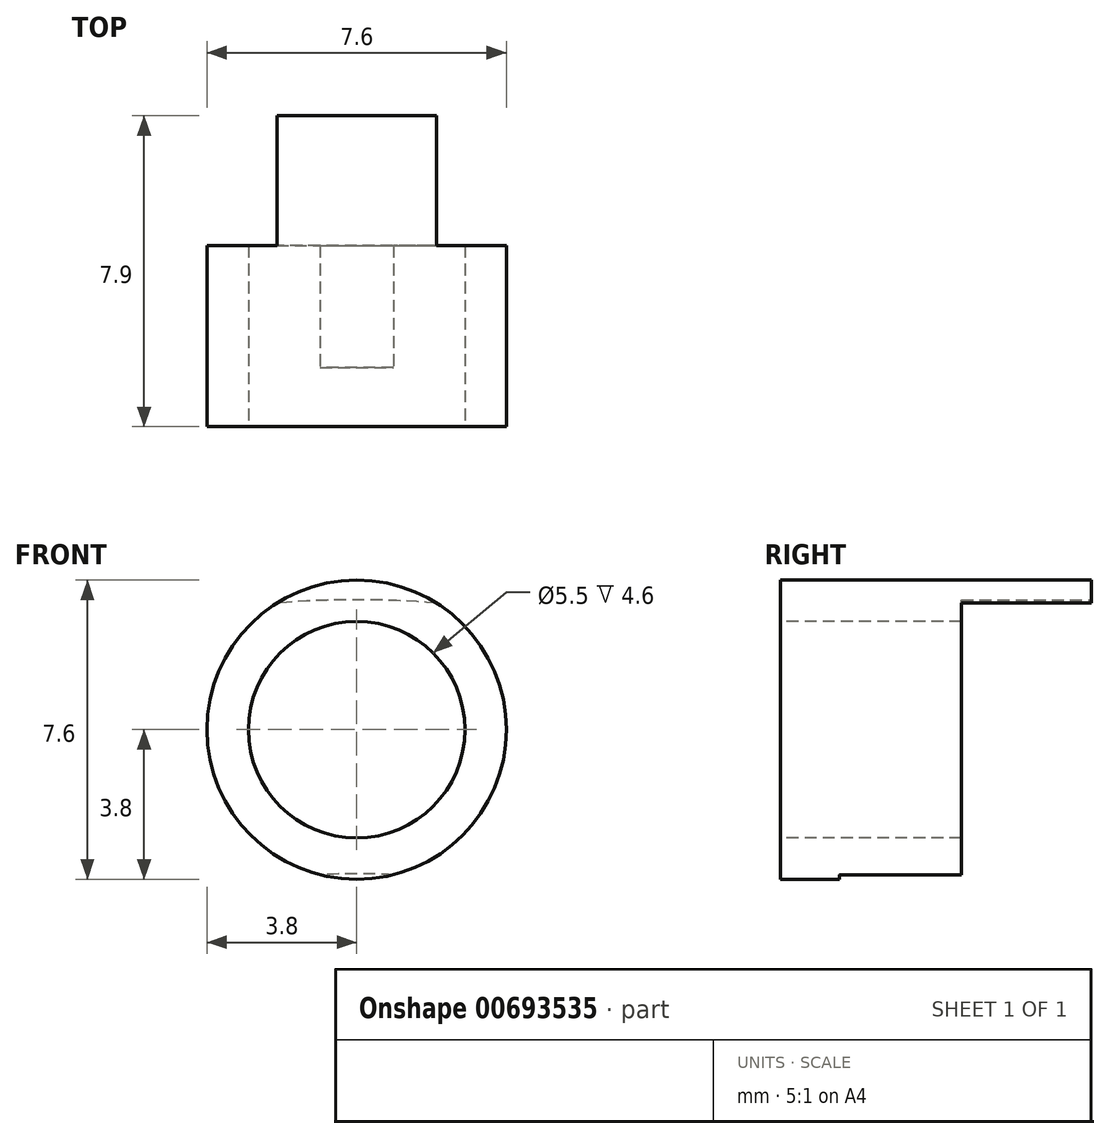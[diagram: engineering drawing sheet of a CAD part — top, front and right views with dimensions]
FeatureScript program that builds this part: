
annotation { "Feature Type Name" : "Feature", "Feature Type Description" : "" }
export const myFeature = defineFeature(function(context is Context, id is Id, definition is map)
    precondition{}
    {
        {
            var Q0;
            Q0=qCreatedBy(makeId("Front.planeOp"),FACE);
            var sketch = newSketch(context, id + "F0", { "sketchPlane" : qUnion([Q0])});
            skCircle(sketch, "E0", {"center": v(0, 0) * mm, "radius": 15.72 * mm});
            skCircle(sketch, "E1", {"center": v(0, 0) * mm, "radius": 26.35 * mm});
            skSolve(sketch);
        }
        {
            var Q0;
            Q0=makeQuery(id+"F0.imprint","IMPRINT",FACE,{"disambiguationData":[TD([[makeQuery(id+"F0.imprint","IMPRINT",EDGE,{"derivedFrom":sQuery(id+"F0.wireOp",EDGE,"E0")}),-1.0]])]});
            extrude(context, id + "F1", {"entities" : qUnion([Q0]), "depth" : 11.3 * mm, "offsetDistance" : 25 * mm});
        }
        {
            var Q0;
            Q0=makeQuery(id+"F1.opExtrude","CAP_FACE",FACE,{"disambiguationData":[OSD([sQuery(id+"F0.wireOp",EDGE,"E0"),sQuery(id+"F0.wireOp",EDGE,"E1")])],"isStart":true});
            var sketch = newSketch(context, id + "F2", { "sketchPlane" : qUnion([Q0])});
            skCircle(sketch, "E2", {"center": v(0, 0) * mm, "radius": 17.39 * mm});
            skSolve(sketch);
        }
        {
            var Q0;
            Q0=makeQuery(id+"F2.imprint","IMPRINT",FACE,{"disambiguationData":[TD([[makeQuery(id+"F2.imprint","IMPRINT",EDGE,{"derivedFrom":sQuery(id+"F2.wireOp",EDGE,"E2")}),1.0]])]});
            extrude(context, id + "F3", {"entities" : qUnion([Q0]), "operationType" : NewBodyOperationType.REMOVE, "oppositeDirection" : true, "depth" : 6.4 * mm, "offsetDistance" : 25 * mm});
        }
        {
            var Q0;
            Q0=makeQuery(id+"F1.opExtrude","CAP_FACE",FACE,{"disambiguationData":[OSD([sQuery(id+"F0.wireOp",EDGE,"E0"),sQuery(id+"F0.wireOp",EDGE,"E1")])],"isStart":true});
            var sketch = newSketch(context, id + "F4", { "sketchPlane" : qUnion([Q0])});
            skCircle(sketch, "E3", {"center": v(0, 0) * mm, "radius": 24.35 * mm});
            skSolve(sketch);
        }
        {
            var Q0;
            Q0=makeQuery(id+"F4.imprint","IMPRINT",FACE,{"disambiguationData":[TD([[makeQuery(id+"F4.imprint","IMPRINT",EDGE,{"derivedFrom":sQuery(id+"F4.wireOp",EDGE,"E3")}),1.0]])]});
            extrude(context, id + "F5", {"entities" : qUnion([Q0]), "operationType" : NewBodyOperationType.REMOVE, "oppositeDirection" : true, "depth" : 3.3 * mm, "offsetDistance" : 25 * mm});
        }
        {
            var Q0;
            Q0=makeQuery(id+"F1.opExtrude","CAP_FACE",FACE,{"disambiguationData":[OSD([sQuery(id+"F0.wireOp",EDGE,"E0"),sQuery(id+"F0.wireOp",EDGE,"E1")])],"isStart":false});
            var sketch = newSketch(context, id + "F6", { "sketchPlane" : qUnion([Q0])});
            skCircle(sketch, "E4", {"center": v(0, 21.05) * mm, "radius": 2.75 * mm});
            skCircle(sketch, "E5", {"center": v(0, 21.05) * mm, "radius": 3.8 * mm});
            skSolve(sketch);
        }
        {
            var Q0;
            Q0=makeQuery(id+"F6.imprint","IMPRINT",FACE,{"disambiguationData":[TD([[makeQuery(id+"F6.imprint","IMPRINT",EDGE,{"derivedFrom":sQuery(id+"F6.wireOp",EDGE,"E4")}),-1.0]])]});
            extrude(context, id + "F7", {"entities" : qUnion([Q0]), "operationType" : NewBodyOperationType.REMOVE, "oppositeDirection" : true, "depth" : 3.4 * mm, "offsetDistance" : 25 * mm});
        }
        {
            var Q0;
            Q0=makeQuery(id+"F7.boolean.opBoolean","SPLIT",FACE,{"disambiguationData":[TD([makeQuery(id+"F7.opExtrude","SWEPT_FACE",FACE,{"disambiguationData":[OSD([sQuery(id+"F6.wireOp",EDGE,"E4")])]})])],"derivedFrom":makeQuery(id+"F1.opExtrude","CAP_FACE",FACE,{"disambiguationData":[OSD([sQuery(id+"F0.wireOp",EDGE,"E0"),sQuery(id+"F0.wireOp",EDGE,"E1")])],"isStart":false})});
            extrude(context, id + "F8", {"entities" : qUnion([Q0]), "operationType" : NewBodyOperationType.REMOVE, "oppositeDirection" : true, "depth" : 10 * mm, "offsetDistance" : 25 * mm});
        }
        {
            var Q0;
            Q0=qCreatedBy(makeId("Right.planeOp"),FACE);
            var sketch = newSketch(context, id + "F9", { "sketchPlane" : qUnion([Q0])});
            skLineSegment(sketch, "E6", {"start": v(37.37, 0) * mm, "end": v(-51.59, 0) * mm});
            skSolve(sketch);
        }
        {
            var Q0;
            {var subQ0=sQuery(id+"F0.wireOp",EDGE,"E0");var subQ1=sQuery(id+"F0.wireOp",EDGE,"E1");Q0=makeQuery(id+"FGy4sFd92jukGps_1.1.F7.boolean.opBoolean","SPLIT",FACE,{"disambiguationData":[TD([makeQuery(id+"FGy4sFd92jukGps_1.1.F7.opExtrude","SWEPT_FACE",FACE,{"disambiguationData":[OSD([sQuery(id+"F6.wireOp",EDGE,"E4")])]})])],"derivedFrom":makeQuery(id+"F7.boolean.opBoolean","SPLIT",FACE,{"disambiguationData":[TD([makeQuery(id+"F1.opExtrude","SWEPT_FACE",FACE,{"disambiguationData":[OSD([subQ0])]})])],"derivedFrom":makeQuery(id+"F1.opExtrude","CAP_FACE",FACE,{"disambiguationData":[OSD([subQ0,subQ1])],"isStart":false})})});}
            var Q1;
            {var subQ0=sQuery(id+"F0.wireOp",EDGE,"E0");var subQ1=makeQuery(id+"F1.opExtrude","SWEPT_FACE",FACE,{"disambiguationData":[OSD([subQ0])]});var subQ2=sQuery(id+"F0.wireOp",EDGE,"E1");Q1=makeQuery(id+"FGy4sFd92jukGps_1.2.F7.boolean.opBoolean","SPLIT",FACE,{"disambiguationData":[TD([makeQuery(id+"FGy4sFd92jukGps_1.2.F7.opExtrude","SWEPT_FACE",FACE,{"disambiguationData":[OSD([sQuery(id+"F6.wireOp",EDGE,"E4")])]})])],"derivedFrom":makeQuery(id+"FGy4sFd92jukGps_1.1.F7.boolean.opBoolean","SPLIT",FACE,{"disambiguationData":[TD([subQ1])],"derivedFrom":makeQuery(id+"F7.boolean.opBoolean","SPLIT",FACE,{"disambiguationData":[TD([subQ1])],"derivedFrom":makeQuery(id+"F1.opExtrude","CAP_FACE",FACE,{"disambiguationData":[OSD([subQ0,subQ2])],"isStart":false})})})});}
            extrude(context, id + "F10", {"entities" : qUnion([Q0, Q1]), "operationType" : NewBodyOperationType.REMOVE, "oppositeDirection" : true, "depth" : 25 * mm, "offsetDistance" : 25 * mm});
        }
    });
